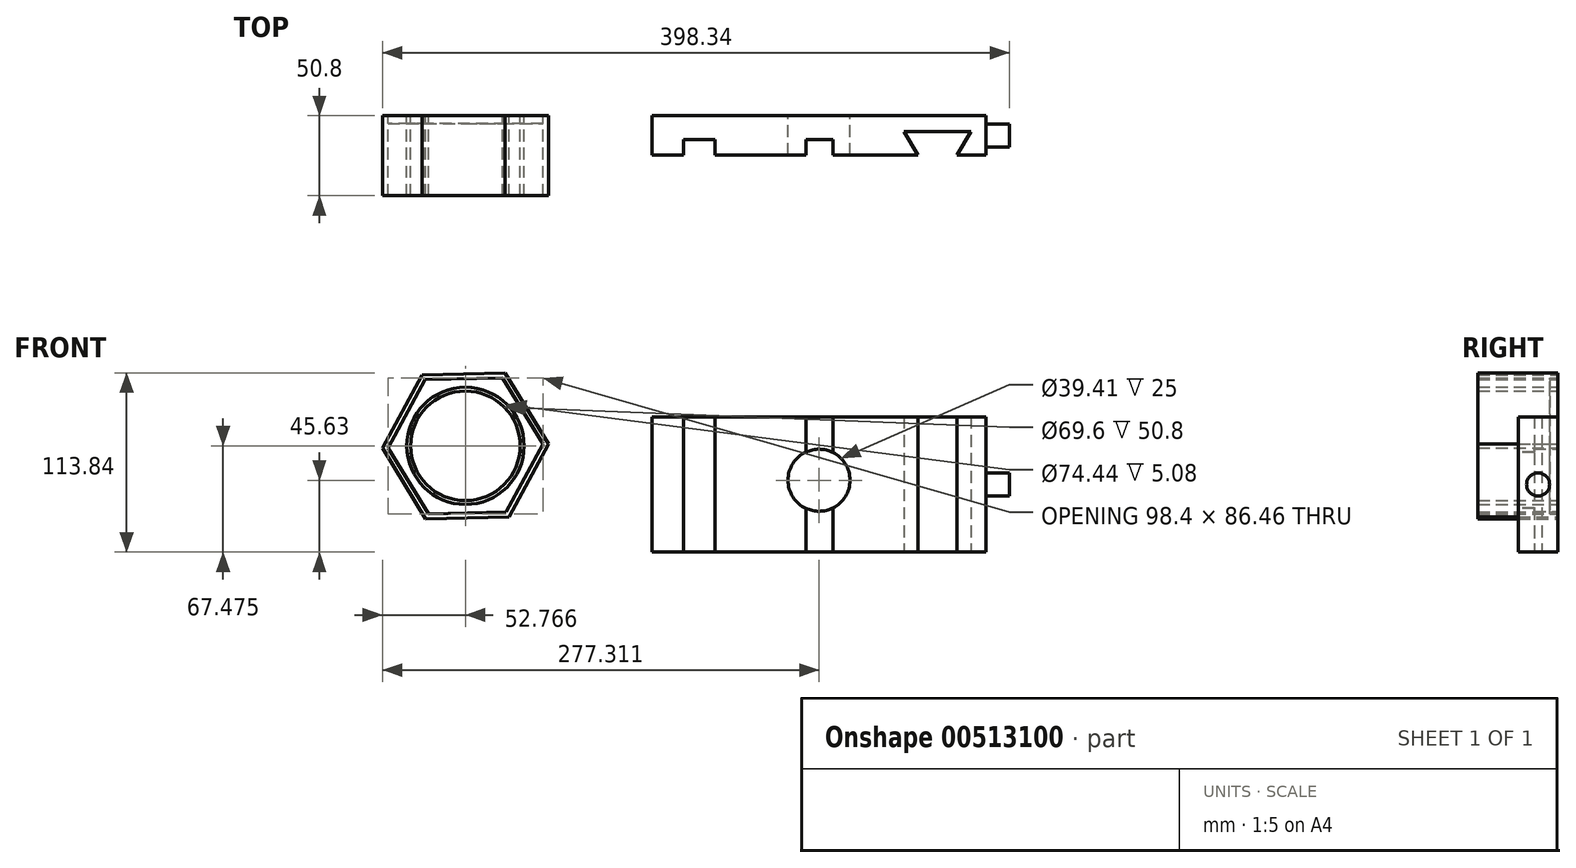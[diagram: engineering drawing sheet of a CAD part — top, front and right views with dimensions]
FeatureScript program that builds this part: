
annotation { "Feature Type Name" : "Feature", "Feature Type Description" : "" }
export const myFeature = defineFeature(function(context is Context, id is Id, definition is map)
    precondition{}
    {
        {
            var Q0;
            Q0=qCreatedBy(makeId("Front.planeOp"),FACE);
            var sketch = newSketch(context, id + "F0", { "sketchPlane" : qUnion([Q0])});
            skCircle(sketch, "E0", {"center": v(-216.22, 21.85) * mm, "radius": 37.22 * mm});
            skCircle(sketch, "E1.cCircle", {"center": v(-216.22, 21.85) * mm, "radius": 45.71 * mm, "construction": true});
            skLineSegment(sketch, "E1.0", {"start": v(-163.46, 23.18) * mm, "end": v(-188.68, -23.18) * mm});
            skLineSegment(sketch, "E1.1", {"start": v(-188.68, -23.18) * mm, "end": v(-241.45, -24.52) * mm});
            skLineSegment(sketch, "E1.2", {"start": v(-241.45, -24.52) * mm, "end": v(-269, 20.5) * mm});
            skLineSegment(sketch, "E1.3", {"start": v(-269, 20.5) * mm, "end": v(-243.77, 66.87) * mm});
            skLineSegment(sketch, "E1.4", {"start": v(-243.77, 66.87) * mm, "end": v(-191, 68.21) * mm});
            skLineSegment(sketch, "E1.5", {"start": v(-191, 68.21) * mm, "end": v(-163.46, 23.18) * mm});
            skPoint(sketch, "E1.0.midPoint", {"position": v(-176.07, 0) * mm});
            skCircle(sketch, "E2.cCircle", {"center": v(-216.22, 21.85) * mm, "radius": 42.62 * mm, "construction": true});
            skLineSegment(sketch, "E2.0", {"start": v(-167.03, 23.1) * mm, "end": v(-190.54, -20.14) * mm});
            skLineSegment(sketch, "E2.1", {"start": v(-190.54, -20.14) * mm, "end": v(-239.74, -21.39) * mm});
            skLineSegment(sketch, "E2.2", {"start": v(-239.74, -21.39) * mm, "end": v(-265.42, 20.6) * mm});
            skLineSegment(sketch, "E2.3", {"start": v(-265.42, 20.6) * mm, "end": v(-241.9, 63.83) * mm});
            skLineSegment(sketch, "E2.4", {"start": v(-241.9, 63.83) * mm, "end": v(-192.7, 65.08) * mm});
            skLineSegment(sketch, "E2.5", {"start": v(-192.7, 65.08) * mm, "end": v(-167.03, 23.1) * mm});
            skPoint(sketch, "E2.0.midPoint", {"position": v(-178.79, 1.48) * mm});
            skCircle(sketch, "E3", {"center": v(-216.22, 21.85) * mm, "radius": 34.8 * mm});
            skSolve(sketch);
        }
        {
            var Q0;
            Q0=makeQuery(id+"F0.imprint","IMPRINT",FACE,{"disambiguationData":[TD([[makeQuery(id+"F0.imprint","IMPRINT",EDGE,{"derivedFrom":sQuery(id+"F0.wireOp",EDGE,"E1.0")}),-1.0]])]});
            extrude(context, id + "F1", {"entities" : qUnion([Q0]), "depth" : 50.8 * mm, "offsetDistance" : 25.4 * mm});
        }
        {
            var Q0;
            Q0=makeQuery(id+"F0.imprint","IMPRINT",FACE,{"disambiguationData":[TD([[makeQuery(id+"F0.imprint","IMPRINT",EDGE,{"derivedFrom":sQuery(id+"F0.wireOp",EDGE,"E0")}),1.0]])]});
            extrude(context, id + "F2", {"entities" : qUnion([Q0]), "depth" : 50.8 * mm, "offsetDistance" : 25.4 * mm});
        }
        {
            var Q0;
            Q0=makeQuery(id+"F0.imprint","IMPRINT",FACE,{"disambiguationData":[TD([[makeQuery(id+"F0.imprint","IMPRINT",EDGE,{"derivedFrom":sQuery(id+"F0.wireOp",EDGE,"E0")}),-1.0]])]});
            extrude(context, id + "F3", {"entities" : qUnion([Q0]), "depth" : 5.08 * mm, "offsetDistance" : 25.4 * mm});
        }
        {
            var Q0;
            Q0=qCreatedBy(makeId("Front.planeOp"),FACE);
            var sketch = newSketch(context, id + "F4", { "sketchPlane" : qUnion([Q0])});
            skLineSegment(sketch, "E4.bottom", {"start": v(-97.7, 40.26) * mm, "end": v(114.35, 40.26) * mm});
            skLineSegment(sketch, "E4.top", {"start": v(-97.7, -45.63) * mm, "end": v(114.35, -45.63) * mm});
            skLineSegment(sketch, "E4.left", {"start": v(-97.7, 40.26) * mm, "end": v(-97.7, -45.63) * mm});
            skLineSegment(sketch, "E4.right", {"start": v(114.35, 40.26) * mm, "end": v(114.35, -45.63) * mm});
            skCircle(sketch, "E5", {"center": v(8.32, 0) * mm, "radius": 19.7 * mm});
            skPoint(sketch, "E5.centerSnap0", {"position": v(8.32, 40.26) * mm});
            skSolve(sketch);
        }
        {
            var Q0;
            Q0=makeQuery(id+"F4.imprint","IMPRINT",FACE,{"disambiguationData":[TD([[makeQuery(id+"F4.imprint","IMPRINT",EDGE,{"derivedFrom":sQuery(id+"F4.wireOp",EDGE,"E4.bottom")}),-1.0]])]});
            extrude(context, id + "F5", {"entities" : qUnion([Q0]), "depth" : 25 * mm, "offsetDistance" : 25 * mm});
        }
        {
            var Q0;
            Q0=makeQuery(id+"F5.opExtrude","CAP_FACE",FACE,{"disambiguationData":[OSD([sQuery(id+"F4.wireOp",EDGE,"E4.bottom"),sQuery(id+"F4.wireOp",EDGE,"E4.top"),sQuery(id+"F4.wireOp",EDGE,"E4.left"),sQuery(id+"F4.wireOp",EDGE,"E4.right"),sQuery(id+"F4.wireOp",EDGE,"E5")])],"isStart":false});
            var sketch = newSketch(context, id + "F6", { "sketchPlane" : qUnion([Q0])});
            skLineSegment(sketch, "E6.bottom", {"start": v(-77.7, 40.26) * mm, "end": v(-57.7, 40.26) * mm});
            skLineSegment(sketch, "E6.top", {"start": v(-77.7, -45.63) * mm, "end": v(-57.7, -45.63) * mm});
            skLineSegment(sketch, "E6.left", {"start": v(-77.7, 40.26) * mm, "end": v(-77.7, -45.63) * mm});
            skLineSegment(sketch, "E6.right", {"start": v(-57.7, 40.26) * mm, "end": v(-57.7, -45.63) * mm});
            skLineSegment(sketch, "E7", {"start": v(0.07, 40.26) * mm, "end": v(0.07, -45.63) * mm});
            skLineSegment(sketch, "E8", {"start": v(17.15, 40.26) * mm, "end": v(17.15, -45.63) * mm});
            skPoint(sketch, "E9", {"position": v(8.32, 0) * mm});
            skLineSegment(sketch, "E10", {"start": v(8.32, 40.26) * mm, "end": v(8.32, -45.63) * mm, "construction": true});
            skSolve(sketch);
        }
        {
            var Q0;
            Q0=makeQuery(id+"F6.imprint","IMPRINT",FACE,{"disambiguationData":[TD([[makeQuery(id+"F6.imprint","IMPRINT",EDGE,{"derivedFrom":sQuery(id+"F6.wireOp",EDGE,"E6.bottom")}),-1.0]])]});
            var Q1;
            {var subQ0=sQuery(id+"F6.wireOp",EDGE,"E7");var subQ1=makeQuery(id+"F5.opExtrude","CAP_EDGE",EDGE,{"disambiguationData":[OSD([sQuery(id+"F4.wireOp",EDGE,"E4.top")])],"isStart":false});var subQ2=makeQuery(id+"F6.imprint","INTERSECT",VERTEX,{"derivedFrom":[subQ1,subQ0]});Q1=makeQuery(id+"F6.imprint","IMPRINT",FACE,{"disambiguationData":[TD([[makeQuery(id+"F6.imprint","IMPRINT",EDGE,{"disambiguationData":[TD([[subQ2,1.0]])],"derivedFrom":subQ0}),1.0]])]});}
            var Q2;
            {var subQ0=sQuery(id+"F6.wireOp",EDGE,"E7");var subQ1=makeQuery(id+"F5.opExtrude","CAP_EDGE",EDGE,{"disambiguationData":[OSD([sQuery(id+"F4.wireOp",EDGE,"E4.bottom")])],"isStart":false});var subQ2=makeQuery(id+"F6.imprint","INTERSECT",VERTEX,{"derivedFrom":[subQ1,subQ0]});Q2=makeQuery(id+"F6.imprint","IMPRINT",FACE,{"disambiguationData":[TD([[makeQuery(id+"F6.imprint","IMPRINT",EDGE,{"disambiguationData":[TD([[subQ2,-1.0]])],"derivedFrom":subQ0}),1.0]])]});}
            extrude(context, id + "F7", {"entities" : qUnion([Q0, Q1, Q2]), "operationType" : NewBodyOperationType.REMOVE, "oppositeDirection" : true, "depth" : 10 * mm, "offsetDistance" : 25 * mm});
        }
        {
            var Q0;
            Q0=makeQuery(id+"F5.opExtrude","SWEPT_FACE",FACE,{"disambiguationData":[OSD([sQuery(id+"F4.wireOp",EDGE,"E4.top")])]});
            var sketch = newSketch(context, id + "F8", { "sketchPlane" : qUnion([Q0])});
            skLineSegment(sketch, "E11", {"start": v(71.1, 25) * mm, "end": v(62.45, 10) * mm});
            skLineSegment(sketch, "E12", {"start": v(62.45, 10) * mm, "end": v(104.77, 10) * mm});
            skLineSegment(sketch, "E13", {"start": v(104.77, 10) * mm, "end": v(96.1, 25) * mm});
            skLineSegment(sketch, "E14", {"start": v(96.1, 25) * mm, "end": v(71.1, 25) * mm});
            skLineSegment(sketch, "E15", {"start": v(83.6, 10) * mm, "end": v(83.6, 25) * mm, "construction": true});
            skSolve(sketch);
        }
        {
            var Q0;
            Q0=makeQuery(id+"F8.imprint","IMPRINT",FACE,{"disambiguationData":[TD([[makeQuery(id+"F8.imprint","IMPRINT",EDGE,{"derivedFrom":sQuery(id+"F8.wireOp",EDGE,"E11")}),1.0]])]});
            extrude(context, id + "F9", {"entities" : qUnion([Q0]), "operationType" : NewBodyOperationType.REMOVE, "endBound" : BoundingType.THROUGH_ALL, "oppositeDirection" : true, "depth" : 25 * mm, "offsetDistance" : 25 * mm});
        }
        {
            var Q0;
            Q0=makeQuery(id+"F5.opExtrude","SWEPT_FACE",FACE,{"disambiguationData":[OSD([sQuery(id+"F4.wireOp",EDGE,"E4.right")])]});
            var sketch = newSketch(context, id + "F10", { "sketchPlane" : qUnion([Q0])});
            skCircle(sketch, "E16", {"center": v(-12.5, -2.68) * mm, "radius": 7.33 * mm});
            skPoint(sketch, "E16.centerSnap0", {"position": v(-12.5, -45.63) * mm});
            skPoint(sketch, "E16.centerSnap1", {"position": v(-25, -2.68) * mm});
            skSolve(sketch);
        }
        {
            var Q0;
            Q0=makeQuery(id+"F10.imprint","IMPRINT",FACE,{"disambiguationData":[TD([[makeQuery(id+"F10.imprint","IMPRINT",EDGE,{"derivedFrom":sQuery(id+"F10.wireOp",EDGE,"E16")}),1.0]])]});
            extrude(context, id + "F11", {"entities" : qUnion([Q0]), "operationType" : NewBodyOperationType.ADD, "depth" : 15 * mm, "offsetDistance" : 25 * mm});
        }
    });
